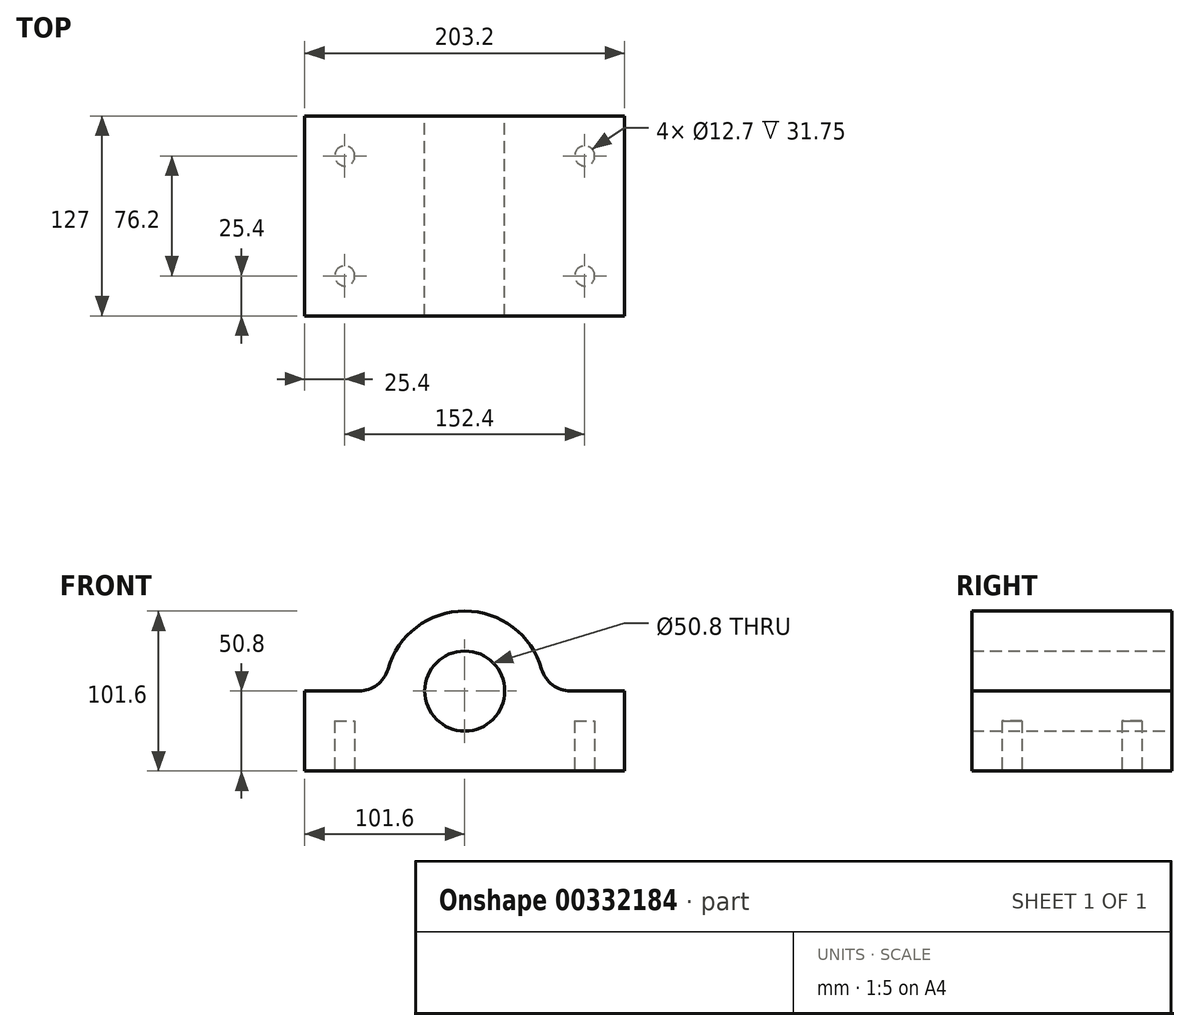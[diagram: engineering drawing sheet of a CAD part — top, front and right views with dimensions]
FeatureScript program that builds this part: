
annotation { "Feature Type Name" : "Feature", "Feature Type Description" : "" }
export const myFeature = defineFeature(function(context is Context, id is Id, definition is map)
    precondition{}
    {
        {
            var Q0;
            Q0=qCreatedBy(makeId("Front.planeOp"),FACE);
            var sketch = newSketch(context, id + "F0", { "sketchPlane" : qUnion([Q0])});
            skCircle(sketch, "E0", {"center": v(0, 0) * mm, "radius": 25.4 * mm});
            skArc(sketch, "E1", {"start": v(48.87, 13.85) * mm, "mid": v(0, 50.8) * mm, "end": v(-48.87, 13.85) * mm});
            skLineSegment(sketch, "E2", {"start": v(0, 0) * mm, "end": v(25.4, 0) * mm});
            skLineSegment(sketch, "E3", {"start": v(101.6, 0) * mm, "end": v(101.6, -50.8) * mm});
            skLineSegment(sketch, "E4", {"start": v(101.6, -50.8) * mm, "end": v(-101.6, -50.8) * mm});
            skLineSegment(sketch, "E5", {"start": v(-101.6, -50.8) * mm, "end": v(-101.6, 0) * mm});
            skLineSegment(sketch, "E6", {"start": v(-101.6, 0) * mm, "end": v(-67.2, 0) * mm});
            skArc(sketch, "E7", {"start": v(48.87, 13.85) * mm, "mid": v(55.71, 3.85) * mm, "end": v(67.2, 0) * mm});
            skArc(sketch, "E8", {"start": v(-67.2, 0) * mm, "mid": v(-55.71, 3.85) * mm, "end": v(-48.87, 13.85) * mm});
            skLineSegment(sketch, "E9.trimOffspring", {"start": v(67.2, 0) * mm, "end": v(101.6, 0) * mm});
            skLineSegment(sketch, "E10.trimOffspring", {"start": v(-25.4, 0) * mm, "end": v(0, 0) * mm});
            skSolve(sketch);
        }
        {
            var Q0;
            Q0=makeQuery(id+"F0.imprint","IMPRINT",FACE,{"disambiguationData":[TD([[makeQuery(id+"F0.imprint","IMPRINT",EDGE,{"derivedFrom":sQuery(id+"F0.wireOp",EDGE,"E1")}),1.0]])]});
            extrude(context, id + "F1", {"entities" : qUnion([Q0]), "depth" : 127 * mm});
        }
        {
            var Q0;
            Q0=makeQuery(id+"F1.opExtrude","SWEPT_FACE",FACE,{"disambiguationData":[OSD([sQuery(id+"F0.wireOp",EDGE,"E4")])]});
            var sketch = newSketch(context, id + "F2", { "sketchPlane" : qUnion([Q0])});
            skCircle(sketch, "E11", {"center": v(76.2, 101.6) * mm, "radius": 6.35 * mm});
            skCircle(sketch, "E12", {"center": v(76.2, 25.4) * mm, "radius": 6.35 * mm});
            skCircle(sketch, "E13", {"center": v(-76.2, 101.6) * mm, "radius": 6.35 * mm});
            skCircle(sketch, "E14", {"center": v(-76.2, 25.4) * mm, "radius": 6.35 * mm});
            skSolve(sketch);
        }
        {
            var Q0;
            Q0=makeQuery(id+"F2.imprint","IMPRINT",FACE,{"disambiguationData":[TD([[makeQuery(id+"F2.imprint","IMPRINT",EDGE,{"derivedFrom":sQuery(id+"F2.wireOp",EDGE,"E13")}),1.0]])]});
            var Q1;
            Q1=makeQuery(id+"F2.imprint","IMPRINT",FACE,{"disambiguationData":[TD([[makeQuery(id+"F2.imprint","IMPRINT",EDGE,{"derivedFrom":sQuery(id+"F2.wireOp",EDGE,"E14")}),1.0]])]});
            var Q2;
            Q2=makeQuery(id+"F2.imprint","IMPRINT",FACE,{"disambiguationData":[TD([[makeQuery(id+"F2.imprint","IMPRINT",EDGE,{"derivedFrom":sQuery(id+"F2.wireOp",EDGE,"E12")}),1.0]])]});
            var Q3;
            Q3=makeQuery(id+"F2.imprint","IMPRINT",FACE,{"disambiguationData":[TD([[makeQuery(id+"F2.imprint","IMPRINT",EDGE,{"derivedFrom":sQuery(id+"F2.wireOp",EDGE,"E11")}),1.0]])]});
            extrude(context, id + "F3", {"entities" : qUnion([Q0, Q1, Q2, Q3]), "operationType" : NewBodyOperationType.REMOVE, "oppositeDirection" : true, "depth" : 31.75 * mm});
        }
    });
